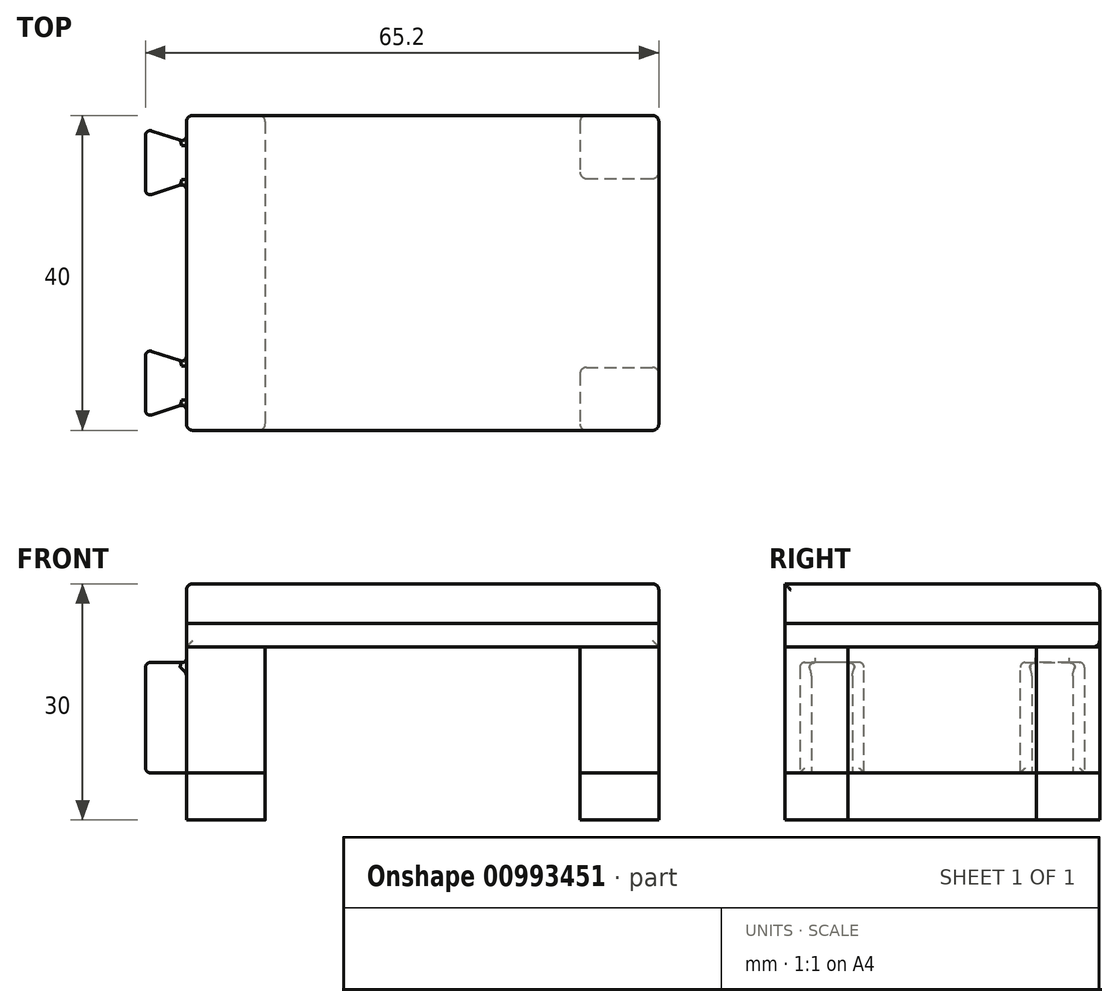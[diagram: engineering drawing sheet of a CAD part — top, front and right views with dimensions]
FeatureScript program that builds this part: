
annotation { "Feature Type Name" : "Feature", "Feature Type Description" : "" }
export const myFeature = defineFeature(function(context is Context, id is Id, definition is map)
    precondition{}
    {
        {
            var Q0;
            Q0=qCreatedBy(makeId("Top.planeOp"),FACE);
            var sketch = newSketch(context, id + "F0", { "sketchPlane" : qUnion([Q0])});
            skLineSegment(sketch, "E0.bottom", {"start": v(-30, 20) * mm, "end": v(-20, 20) * mm});
            skLineSegment(sketch, "E0.top", {"start": v(-30, -20) * mm, "end": v(-20, -20) * mm});
            skLineSegment(sketch, "E0.left", {"start": v(-30, 20) * mm, "end": v(-30, -20) * mm});
            skLineSegment(sketch, "E0.right", {"start": v(-20, 20) * mm, "end": v(-20, -20) * mm});
            skLineSegment(sketch, "E1.bottom", {"start": v(20, 20) * mm, "end": v(30, 20) * mm});
            skLineSegment(sketch, "E1.top", {"start": v(20, -20) * mm, "end": v(30, -20) * mm});
            skLineSegment(sketch, "E1.left", {"start": v(20, 20) * mm, "end": v(20, -20) * mm});
            skLineSegment(sketch, "E1.right", {"start": v(30, 20) * mm, "end": v(30, -20) * mm});
            skLineSegment(sketch, "E2", {"start": v(-20, 0) * mm, "end": v(0, 0) * mm, "construction": true});
            skLineSegment(sketch, "E3", {"start": v(20, 0) * mm, "end": v(0, 0) * mm, "construction": true});
            skLineSegment(sketch, "E4.bottom", {"start": v(20, 12) * mm, "end": v(30, 12) * mm});
            skLineSegment(sketch, "E4.top", {"start": v(20, -12) * mm, "end": v(30, -12) * mm});
            skLineSegment(sketch, "E4.left", {"start": v(20, 12) * mm, "end": v(20, -12) * mm});
            skLineSegment(sketch, "E4.right", {"start": v(30, 12) * mm, "end": v(30, -12) * mm});
            skLineSegment(sketch, "E5", {"start": v(25, 20) * mm, "end": v(25, 12) * mm, "construction": true});
            skLineSegment(sketch, "E6", {"start": v(0, 0) * mm, "end": v(-59.28, 0) * mm, "construction": true});
            skPoint(sketch, "E7", {"position": v(-30, 16.6) * mm});
            skPoint(sketch, "E8", {"position": v(-30, 11.4) * mm});
            skPoint(sketch, "E9", {"position": v(-35.2, 9.7) * mm});
            skPoint(sketch, "E10", {"position": v(-35.2, 18.3) * mm});
            skLineSegment(sketch, "E11", {"start": v(-35.2, 18.3) * mm, "end": v(-30, 16.6) * mm});
            skLineSegment(sketch, "E12", {"start": v(-35.2, 9.7) * mm, "end": v(-35.2, 18.3) * mm});
            skLineSegment(sketch, "E13", {"start": v(-35.2, 9.7) * mm, "end": v(-30, 11.4) * mm});
            skLineSegment(sketch, "E14", {"start": v(-30, 16.6) * mm, "end": v(-30, 11.4) * mm});
            skLineSegment(sketch, "E15", {"start": v(-35.2, 14) * mm, "end": v(-30, 14) * mm, "construction": true});
            skLineSegment(sketch, "E16.MirrorCS", {"start": v(-35.2, -18.3) * mm, "end": v(-30, -16.6) * mm});
            skLineSegment(sketch, "E17.MirrorCS", {"start": v(-35.2, -9.7) * mm, "end": v(-35.2, -18.3) * mm});
            skLineSegment(sketch, "E18.MirrorCS", {"start": v(-35.2, -9.7) * mm, "end": v(-30, -11.4) * mm});
            skLineSegment(sketch, "E19.MirrorCS", {"start": v(-30, -16.6) * mm, "end": v(-30, -11.4) * mm});
            skLineSegment(sketch, "E20.MirrorCS", {"start": v(-35.2, -14) * mm, "end": v(-30, -14) * mm, "construction": true});
            skSolve(sketch);
        }
        {
            var Q0;
            {var subQ0=sQuery(id+"F0.wireOp",EDGE,"E0.top");Q0=makeQuery(id+"F0.imprint","IMPRINT",FACE,{"disambiguationData":[TD([[makeQuery(id+"F0.imprint","IMPRINT",EDGE,{"derivedFrom":subQ0}),1.0]])]});}
            var Q1;
            {var subQ0=sQuery(id+"F0.wireOp",EDGE,"E0.bottom");Q1=makeQuery(id+"F0.imprint","IMPRINT",FACE,{"disambiguationData":[TD([[makeQuery(id+"F0.imprint","IMPRINT",EDGE,{"derivedFrom":subQ0}),-1.0]])]});}
            var Q2;
            {var subQ0=sQuery(id+"F0.wireOp",EDGE,"E1.bottom");Q2=makeQuery(id+"F0.imprint","IMPRINT",FACE,{"disambiguationData":[TD([[makeQuery(id+"F0.imprint","IMPRINT",EDGE,{"derivedFrom":subQ0}),-1.0]])]});}
            var Q3;
            {var subQ0=sQuery(id+"F0.wireOp",EDGE,"E1.top");Q3=makeQuery(id+"F0.imprint","IMPRINT",FACE,{"disambiguationData":[TD([[makeQuery(id+"F0.imprint","IMPRINT",EDGE,{"derivedFrom":subQ0}),1.0]])]});}
            var Q4;
            Q4=makeQuery(id+"F0.imprint","IMPRINT",FACE,{"disambiguationData":[TD([[makeQuery(id+"F0.imprint","IMPRINT",EDGE,{"derivedFrom":sQuery(id+"F0.wireOp",EDGE,"nnUU5Lm5-dtHu-0g4G-YGr4-6AVNyA5VbQTD.bottom")}),-1.0]])]});
            extrude(context, id + "F1", {"entities" : qUnion([Q0, Q1, Q2, Q3, Q4]), "depth" : 16 * mm, "offsetDistance" : 25 * mm});
        }
        {
            var Q0;
            Q0=makeQuery(id+"F0.imprint","IMPRINT",FACE,{"disambiguationData":[TD([[makeQuery(id+"F0.imprint","IMPRINT",EDGE,{"derivedFrom":sQuery(id+"F0.wireOp",EDGE,"E16.MirrorCS")}),1.0]])]});
            var Q1;
            Q1=makeQuery(id+"F0.imprint","IMPRINT",FACE,{"disambiguationData":[TD([[makeQuery(id+"F0.imprint","IMPRINT",EDGE,{"derivedFrom":sQuery(id+"F0.wireOp",EDGE,"E11")}),-1.0]])]});
            extrude(context, id + "F2", {"entities" : qUnion([Q0, Q1]), "operationType" : NewBodyOperationType.ADD, "depth" : 14 * mm, "offsetDistance" : 25 * mm});
        }
        {
            var Q0;
            Q0=makeQuery(id+"F1.opExtrude","CAP_FACE",FACE,{"disambiguationData":[OSD([sQuery(id+"F0.wireOp",EDGE,"E0.bottom"),sQuery(id+"F0.wireOp",EDGE,"E0.top"),sQuery(id+"F0.wireOp",EDGE,"E0.left"),sQuery(id+"F0.wireOp",EDGE,"E0.right"),sQuery(id+"F0.wireOp",EDGE,"E14"),sQuery(id+"F0.wireOp",EDGE,"E19.MirrorCS")])],"isStart":false});
            var sketch = newSketch(context, id + "F3", { "sketchPlane" : qUnion([Q0])});
            skLineSegment(sketch, "E21.bottom", {"start": v(-30, -20) * mm, "end": v(30, -20) * mm});
            skLineSegment(sketch, "E21.top", {"start": v(-30, -20) * mm, "end": v(30, -20) * mm});
            skLineSegment(sketch, "E21.left", {"start": v(-30, -20) * mm, "end": v(-30, -20) * mm});
            skLineSegment(sketch, "E21.right", {"start": v(30, -20) * mm, "end": v(30, -20) * mm});
            skLineSegment(sketch, "E22.bottom", {"start": v(30, 20) * mm, "end": v(-30, 20) * mm});
            skLineSegment(sketch, "E22.top", {"start": v(30, -20) * mm, "end": v(-30, -20) * mm});
            skLineSegment(sketch, "E22.left", {"start": v(30, 20) * mm, "end": v(30, -20) * mm});
            skLineSegment(sketch, "E22.right", {"start": v(-30, 20) * mm, "end": v(-30, -20) * mm});
            skLineSegment(sketch, "E23", {"start": v(0, 20) * mm, "end": v(0, -20) * mm, "construction": true});
            skLineSegment(sketch, "E24", {"start": v(-30, 0) * mm, "end": v(30, 0) * mm, "construction": true});
            skLineSegment(sketch, "E25.MirrorCS", {"start": v(0, -20) * mm, "end": v(0, 20) * mm, "construction": true});
            skSolve(sketch);
        }
        {
            var Q0;
            Q0 = qSketchRegion(id + "F3", true);
            var Q1;
            Q1=makeQuery(id+"F3.imprint","IMPRINT",FACE,{"disambiguationData":[TD([[makeQuery(id+"F3.imprint","IMPRINT",EDGE,{"derivedFrom":sQuery(id+"F3.wireOp",EDGE,"70d6c611-b537-437c-9655-72f3baaeb9d50.MirrorC")}),-1.0]])]});
            var Q2;
            Q2=makeQuery(id+"F3.imprint","IMPRINT",FACE,{"disambiguationData":[TD([[makeQuery(id+"F3.imprint","IMPRINT",EDGE,{"derivedFrom":sQuery(id+"F3.wireOp",EDGE,"93dbfa5d-dbd3-4445-b28d-ae964d6c23f30.MirrorC")}),1.0]])]});
            var Q3;
            Q3=makeQuery(id+"F3.imprint","IMPRINT",FACE,{"disambiguationData":[TD([[makeQuery(id+"F3.imprint","IMPRINT",EDGE,{"derivedFrom":sQuery(id+"F3.wireOp",EDGE,"IjlcNwAI-avI0-1ZiF-ECz7-kY0PJIWta5Dh")}),1.0]])]});
            var Q4;
            Q4=makeQuery(id+"F3.imprint","IMPRINT",FACE,{"disambiguationData":[TD([[makeQuery(id+"F3.imprint","IMPRINT",EDGE,{"derivedFrom":sQuery(id+"F3.wireOp",EDGE,"KF3wbHbO-wrE6-UmuD-fxoE-mf4LOqjEzulU")}),1.0]])]});
            var Q5;
            Q5=makeQuery(id+"F3.imprint","IMPRINT",FACE,{"disambiguationData":[TD([[makeQuery(id+"F3.imprint","IMPRINT",EDGE,{"derivedFrom":sQuery(id+"F3.wireOp",EDGE,"VtyKOhbS-FhKA-jPoV-oSdO-tDhnUCAPANJn")}),1.0]])]});
            var Q6;
            Q6=makeQuery(id+"F3.imprint","IMPRINT",FACE,{"disambiguationData":[TD([[makeQuery(id+"F3.imprint","IMPRINT",EDGE,{"derivedFrom":sQuery(id+"F3.wireOp",EDGE,"OHk5XSgq-2k9W-Yhoc-utun-htaxunfnWzGF")}),1.0]])]});
            extrude(context, id + "F4", {"entities" : qUnion([Q0, Q1, Q2, Q3, Q4, Q5, Q6]), "depth" : 3 * mm, "offsetDistance" : 25 * mm});
        }
        {
            var Q0;
            Q0 = qSketchRegion(id + "F3", true);
            extrude(context, id + "F5", {"entities" : qUnion([Q0]), "depth" : 8 * mm, "offsetDistance" : 25 * mm});
        }
        {
            var Q0;
            {var subQ3=sQuery(id+"F0.wireOp",EDGE,"E0.bottom");Q0=makeQuery(id+"F0.imprint","IMPRINT",FACE,{"disambiguationData":[TD([[makeQuery(id+"F0.imprint","IMPRINT",EDGE,{"derivedFrom":subQ3}),-1.0]])]});}
            var Q1;
            {var subQ0=sQuery(id+"F0.wireOp",EDGE,"E1.top");Q1=makeQuery(id+"F0.imprint","IMPRINT",FACE,{"disambiguationData":[TD([[makeQuery(id+"F0.imprint","IMPRINT",EDGE,{"derivedFrom":subQ0}),1.0]])]});}
            var Q2;
            {var subQ0=sQuery(id+"F0.wireOp",EDGE,"E1.bottom");Q2=makeQuery(id+"F0.imprint","IMPRINT",FACE,{"disambiguationData":[TD([[makeQuery(id+"F0.imprint","IMPRINT",EDGE,{"derivedFrom":subQ0}),-1.0]])]});}
            extrude(context, id + "F6", {"entities" : qUnion([Q0, Q1, Q2]), "depth" : -6 * mm, "offsetDistance" : 25 * mm});
        }
        {
            var Q0;
            Q0=makeQuery(id+"F2.opExtrude","SWEPT_FACE",FACE,{"disambiguationData":[OSD([sQuery(id+"F0.wireOp",EDGE,"E12")])]});
            var Q1;
            Q1=makeQuery(id+"F2.opExtrude","CAP_FACE",FACE,{"disambiguationData":[OSD([sQuery(id+"F0.wireOp",EDGE,"E11"),sQuery(id+"F0.wireOp",EDGE,"E12"),sQuery(id+"F0.wireOp",EDGE,"E13"),sQuery(id+"F0.wireOp",EDGE,"E14")])],"isStart":false});
            var Q2;
            Q2=makeQuery(id+"F2.opExtrude","CAP_FACE",FACE,{"disambiguationData":[OSD([sQuery(id+"F0.wireOp",EDGE,"E16.MirrorCS"),sQuery(id+"F0.wireOp",EDGE,"E17.MirrorCS"),sQuery(id+"F0.wireOp",EDGE,"E18.MirrorCS"),sQuery(id+"F0.wireOp",EDGE,"E19.MirrorCS")])],"isStart":false});
            var Q3;
            Q3=makeQuery(id+"F2.opExtrude","SWEPT_FACE",FACE,{"disambiguationData":[OSD([sQuery(id+"F0.wireOp",EDGE,"E17.MirrorCS")])]});
            fillet(context, id + "F7", {"entities" : qUnion([Q0, Q1, Q2, Q3]), "radius" : 0.6 * mm, "tangentPropagation" : true, "allowEdgeOverflow" : false});
        }
        {
            var Q0;
            Q0=makeQuery(id+"F1.opExtrude","SWEPT_EDGE",EDGE,{"disambiguationData":[OSD([sQuery(id+"F0.wireOp",EDGE,"E1.top"),sQuery(id+"F0.wireOp",EDGE,"E1.right")])]});
            var Q1;
            Q1=makeQuery(id+"F6.opExtrude","SWEPT_EDGE",EDGE,{"disambiguationData":[OSD([sQuery(id+"F0.wireOp",EDGE,"E1.top"),sQuery(id+"F0.wireOp",EDGE,"E1.right")])]});
            var Q2;
            Q2=makeQuery(id+"F1.opExtrude","SWEPT_EDGE",EDGE,{"disambiguationData":[OSD([sQuery(id+"F0.wireOp",EDGE,"E1.right"),sQuery(id+"F0.wireOp",EDGE,"E4.top"),sQuery(id+"F0.wireOp",EDGE,"E4.right")])]});
            var Q3;
            Q3=makeQuery(id+"F6.opExtrude","SWEPT_EDGE",EDGE,{"disambiguationData":[OSD([sQuery(id+"F0.wireOp",EDGE,"E1.right"),sQuery(id+"F0.wireOp",EDGE,"E4.top"),sQuery(id+"F0.wireOp",EDGE,"E4.right")])]});
            var Q4;
            Q4=makeQuery(id+"F6.opExtrude","SWEPT_EDGE",EDGE,{"disambiguationData":[OSD([sQuery(id+"F0.wireOp",EDGE,"E1.top"),sQuery(id+"F0.wireOp",EDGE,"E1.left")])]});
            var Q5;
            Q5=makeQuery(id+"F1.opExtrude","SWEPT_EDGE",EDGE,{"disambiguationData":[OSD([sQuery(id+"F0.wireOp",EDGE,"E1.top"),sQuery(id+"F0.wireOp",EDGE,"E1.left")])]});
            var Q6;
            Q6=makeQuery(id+"F1.opExtrude","SWEPT_EDGE",EDGE,{"disambiguationData":[OSD([sQuery(id+"F0.wireOp",EDGE,"E1.left"),sQuery(id+"F0.wireOp",EDGE,"E4.top"),sQuery(id+"F0.wireOp",EDGE,"E4.left")])]});
            var Q7;
            Q7=makeQuery(id+"F6.opExtrude","SWEPT_EDGE",EDGE,{"disambiguationData":[OSD([sQuery(id+"F0.wireOp",EDGE,"E1.left"),sQuery(id+"F0.wireOp",EDGE,"E4.top"),sQuery(id+"F0.wireOp",EDGE,"E4.left")])]});
            var Q8;
            Q8=makeQuery(id+"F1.opExtrude","SWEPT_EDGE",EDGE,{"disambiguationData":[OSD([sQuery(id+"F0.wireOp",EDGE,"E1.bottom"),sQuery(id+"F0.wireOp",EDGE,"E1.right")])]});
            var Q9;
            Q9=makeQuery(id+"F6.opExtrude","SWEPT_EDGE",EDGE,{"disambiguationData":[OSD([sQuery(id+"F0.wireOp",EDGE,"E1.bottom"),sQuery(id+"F0.wireOp",EDGE,"E1.right")])]});
            var Q10;
            Q10=makeQuery(id+"F6.opExtrude","SWEPT_EDGE",EDGE,{"disambiguationData":[OSD([sQuery(id+"F0.wireOp",EDGE,"E1.right"),sQuery(id+"F0.wireOp",EDGE,"E4.bottom"),sQuery(id+"F0.wireOp",EDGE,"E4.right")])]});
            var Q11;
            Q11=makeQuery(id+"F1.opExtrude","SWEPT_EDGE",EDGE,{"disambiguationData":[OSD([sQuery(id+"F0.wireOp",EDGE,"E1.right"),sQuery(id+"F0.wireOp",EDGE,"E4.bottom"),sQuery(id+"F0.wireOp",EDGE,"E4.right")])]});
            var Q12;
            Q12=makeQuery(id+"F6.opExtrude","SWEPT_EDGE",EDGE,{"disambiguationData":[OSD([sQuery(id+"F0.wireOp",EDGE,"E1.left"),sQuery(id+"F0.wireOp",EDGE,"E4.bottom"),sQuery(id+"F0.wireOp",EDGE,"E4.left")])]});
            var Q13;
            Q13=makeQuery(id+"F1.opExtrude","SWEPT_EDGE",EDGE,{"disambiguationData":[OSD([sQuery(id+"F0.wireOp",EDGE,"E1.left"),sQuery(id+"F0.wireOp",EDGE,"E4.bottom"),sQuery(id+"F0.wireOp",EDGE,"E4.left")])]});
            var Q14;
            Q14=makeQuery(id+"F1.opExtrude","SWEPT_EDGE",EDGE,{"disambiguationData":[OSD([sQuery(id+"F0.wireOp",EDGE,"E1.bottom"),sQuery(id+"F0.wireOp",EDGE,"E1.left")])]});
            var Q15;
            Q15=makeQuery(id+"F6.opExtrude","SWEPT_EDGE",EDGE,{"disambiguationData":[OSD([sQuery(id+"F0.wireOp",EDGE,"E1.bottom"),sQuery(id+"F0.wireOp",EDGE,"E1.left")])]});
            var Q16;
            Q16=makeQuery(id+"F5.opExtrude","CAP_EDGE",EDGE,{"disambiguationData":[OSD([sQuery(id+"F3.wireOp",EDGE,"E22.bottom")])],"isStart":true});
            var Q17;
            Q17=makeQuery(id+"F5.opExtrude","CAP_EDGE",EDGE,{"disambiguationData":[OSD([sQuery(id+"F3.wireOp",EDGE,"E22.bottom")])],"isStart":false});
            var Q18;
            Q18=makeQuery(id+"F5.opExtrude","SWEPT_EDGE",EDGE,{"disambiguationData":[OSD([sQuery(id+"F3.wireOp",EDGE,"E22.bottom"),sQuery(id+"F3.wireOp",EDGE,"E22.left")])]});
            var Q19;
            Q19=makeQuery(id+"F5.opExtrude","CAP_EDGE",EDGE,{"disambiguationData":[OSD([sQuery(id+"F3.wireOp",EDGE,"E22.left")])],"isStart":false});
            var Q20;
            Q20=makeQuery(id+"F1.opExtrude","SWEPT_EDGE",EDGE,{"disambiguationData":[OSD([sQuery(id+"F0.wireOp",EDGE,"E0.bottom"),sQuery(id+"F0.wireOp",EDGE,"E0.right")])]});
            var Q21;
            Q21=makeQuery(id+"F6.opExtrude","SWEPT_EDGE",EDGE,{"disambiguationData":[OSD([sQuery(id+"F0.wireOp",EDGE,"E0.bottom"),sQuery(id+"F0.wireOp",EDGE,"E0.right")])]});
            var Q22;
            Q22=makeQuery(id+"F6.opExtrude","SWEPT_EDGE",EDGE,{"disambiguationData":[OSD([sQuery(id+"F0.wireOp",EDGE,"E0.bottom"),sQuery(id+"F0.wireOp",EDGE,"E0.left")])]});
            var Q23;
            Q23=makeQuery(id+"F1.opExtrude","SWEPT_EDGE",EDGE,{"disambiguationData":[OSD([sQuery(id+"F0.wireOp",EDGE,"E0.bottom"),sQuery(id+"F0.wireOp",EDGE,"E0.left")])]});
            var Q24;
            Q24=makeQuery(id+"F6.opExtrude","SWEPT_EDGE",EDGE,{"disambiguationData":[OSD([sQuery(id+"F0.wireOp",EDGE,"E0.top"),sQuery(id+"F0.wireOp",EDGE,"E0.left")])]});
            var Q25;
            Q25=makeQuery(id+"F1.opExtrude","SWEPT_EDGE",EDGE,{"disambiguationData":[OSD([sQuery(id+"F0.wireOp",EDGE,"E0.top"),sQuery(id+"F0.wireOp",EDGE,"E0.left")])]});
            var Q26;
            Q26=makeQuery(id+"F6.opExtrude","SWEPT_EDGE",EDGE,{"disambiguationData":[OSD([sQuery(id+"F0.wireOp",EDGE,"E0.top"),sQuery(id+"F0.wireOp",EDGE,"E0.right")])]});
            var Q27;
            Q27=makeQuery(id+"F1.opExtrude","SWEPT_EDGE",EDGE,{"disambiguationData":[OSD([sQuery(id+"F0.wireOp",EDGE,"E0.top"),sQuery(id+"F0.wireOp",EDGE,"E0.right")])]});
            var Q28;
            Q28=makeQuery(id+"F5.opExtrude","CAP_EDGE",EDGE,{"disambiguationData":[OSD([sQuery(id+"F3.wireOp",EDGE,"E22.top")])],"isStart":false});
            var Q29;
            Q29=makeQuery(id+"F5.opExtrude","CAP_EDGE",EDGE,{"disambiguationData":[OSD([sQuery(id+"F3.wireOp",EDGE,"E22.right")])],"isStart":false});
            var Q30;
            Q30=makeQuery(id+"F5.opExtrude","SWEPT_EDGE",EDGE,{"disambiguationData":[OSD([sQuery(id+"F3.wireOp",EDGE,"E22.top"),sQuery(id+"F3.wireOp",EDGE,"E22.right")])]});
            var Q31;
            Q31=makeQuery(id+"F5.opExtrude","SWEPT_EDGE",EDGE,{"disambiguationData":[OSD([sQuery(id+"F3.wireOp",EDGE,"E22.bottom"),sQuery(id+"F3.wireOp",EDGE,"E22.right")])]});
            var Q32;
            Q32=makeQuery(id+"F4.opExtrude","SWEPT_EDGE",EDGE,{"disambiguationData":[OSD([sQuery(id+"F3.wireOp",EDGE,"E22.bottom"),sQuery(id+"F3.wireOp",EDGE,"E22.left")])]});
            var Q33;
            Q33=makeQuery(id+"F4.opExtrude","SWEPT_EDGE",EDGE,{"disambiguationData":[OSD([sQuery(id+"F3.wireOp",EDGE,"E22.top"),sQuery(id+"F3.wireOp",EDGE,"E22.left")])]});
            var Q34;
            Q34=makeQuery(id+"F5.opExtrude","SWEPT_EDGE",EDGE,{"disambiguationData":[OSD([sQuery(id+"F3.wireOp",EDGE,"E22.top"),sQuery(id+"F3.wireOp",EDGE,"E22.left")])]});
            var Q35;
            Q35=makeQuery(id+"F4.opExtrude","SWEPT_EDGE",EDGE,{"disambiguationData":[OSD([sQuery(id+"F3.wireOp",EDGE,"E22.bottom"),sQuery(id+"F3.wireOp",EDGE,"E22.right")])]});
            var Q36;
            Q36=makeQuery(id+"F4.opExtrude","SWEPT_EDGE",EDGE,{"disambiguationData":[OSD([sQuery(id+"F3.wireOp",EDGE,"E22.top"),sQuery(id+"F3.wireOp",EDGE,"E22.right")])]});
            fillet(context, id + "F8", {"entities" : qUnion([Q0, Q1, Q2, Q3, Q4, Q5, Q6, Q7, Q8, Q9, Q10, Q11, Q12, Q13, Q14, Q15, Q16, Q17, Q18, Q19, Q20, Q21, Q22, Q23, Q24, Q25, Q26, Q27, Q28, Q29, Q30, Q31, Q32, Q33, Q34, Q35, Q36]), "radius" : 0.8 * mm, "tangentPropagation" : true, "defaultsChanged" : false, "vertexSettings" : [], "allowEdgeOverflow" : false});
        }
    });
